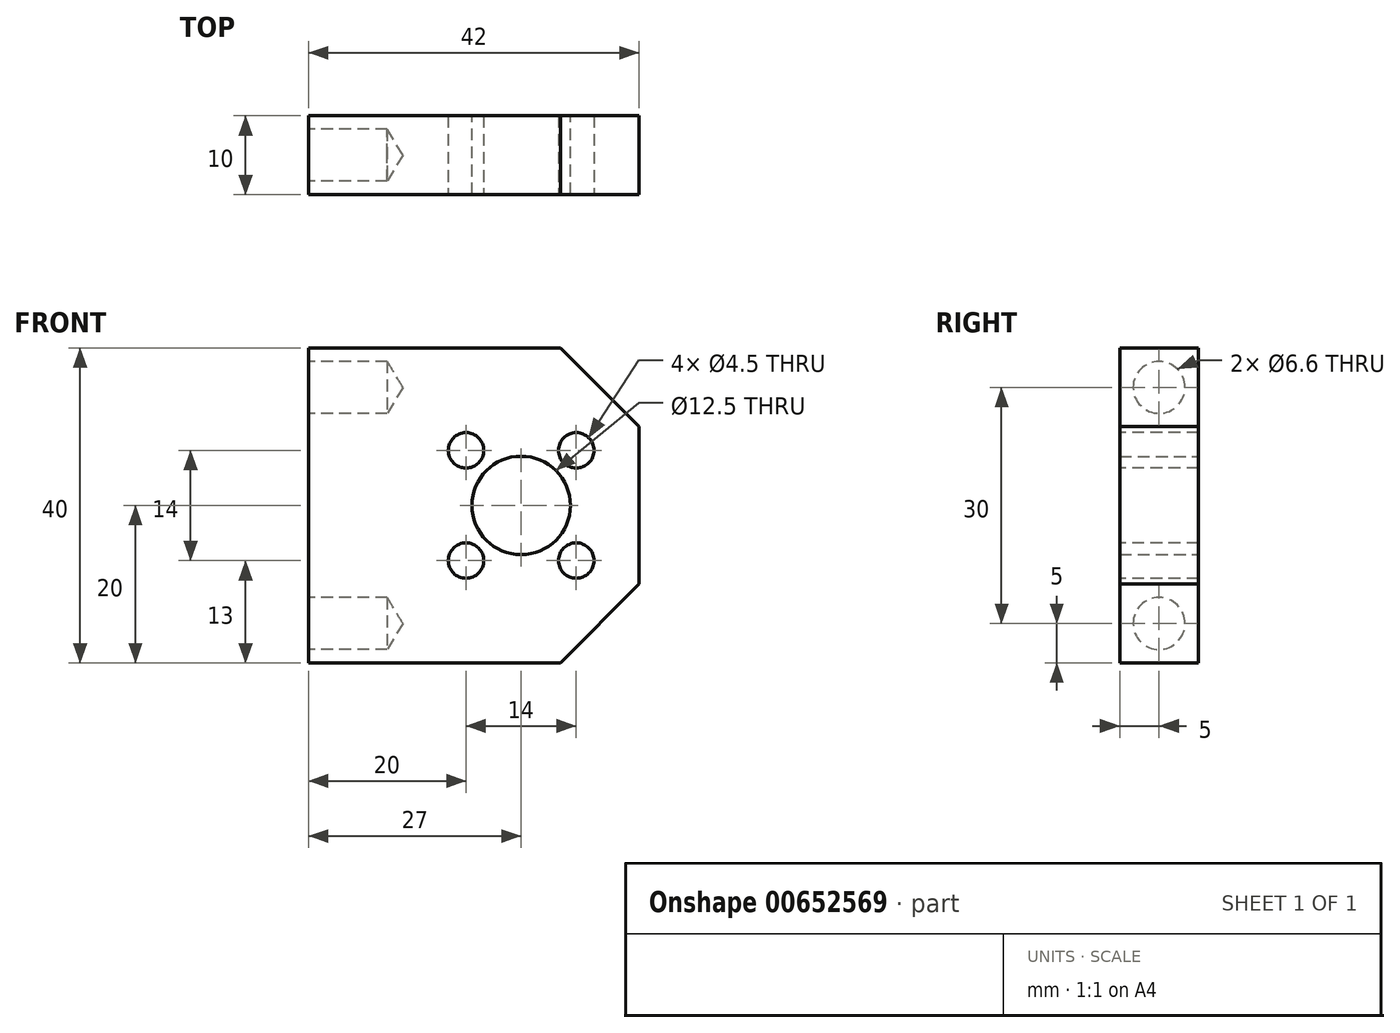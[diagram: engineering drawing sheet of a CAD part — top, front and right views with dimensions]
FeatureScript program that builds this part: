
annotation { "Feature Type Name" : "Feature", "Feature Type Description" : "" }
export const myFeature = defineFeature(function(context is Context, id is Id, definition is map)
    precondition{}
    {
        {
            var Q0;
            Q0=qCreatedBy(makeId("Front.planeOp"),FACE);
            var sketch = newSketch(context, id + "F0", { "sketchPlane" : qUnion([Q0])});
            skLineSegment(sketch, "E0.bottom", {"start": v(21, 20) * mm, "end": v(-21, 20) * mm});
            skLineSegment(sketch, "E0.top", {"start": v(21, -20) * mm, "end": v(-21, -20) * mm});
            skLineSegment(sketch, "E0.left", {"start": v(21, 20) * mm, "end": v(21, -20) * mm});
            skLineSegment(sketch, "E0.right", {"start": v(-21, 20) * mm, "end": v(-21, -20) * mm});
            skPoint(sketch, "E0.middle", {"position": v(0, 0) * mm});
            skCircle(sketch, "E1", {"center": v(6, 0) * mm, "radius": 6.25 * mm});
            skSolve(sketch);
        }
        {
            var Q0;
            Q0 = qSketchRegion(id + "F0", true);
            extrude(context, id + "F1", {"entities" : qUnion([Q0]), "depth" : 10 * mm, "offsetDistance" : 25 * mm});
        }
        {
            var Q0;
            Q0=makeQuery(id+"F1.opExtrude","SWEPT_EDGE",EDGE,{"disambiguationData":[OSD([sQuery(id+"F0.wireOp",EDGE,"E0.bottom"),sQuery(id+"F0.wireOp",EDGE,"E0.left")])]});
            var Q1;
            Q1=makeQuery(id+"F1.opExtrude","SWEPT_EDGE",EDGE,{"disambiguationData":[OSD([sQuery(id+"F0.wireOp",EDGE,"E0.top"),sQuery(id+"F0.wireOp",EDGE,"E0.left")])]});
            chamfer(context, id + "F2", {"entities" : qUnion([Q0, Q1]), "width" : 10 * mm, "tangentPropagation" : true});
        }
        {
            var Q0;
            Q0=makeQuery(id+"F1.opExtrude","CAP_FACE",FACE,{"disambiguationData":[OSD([sQuery(id+"F0.wireOp",EDGE,"E0.bottom"),sQuery(id+"F0.wireOp",EDGE,"E0.top"),sQuery(id+"F0.wireOp",EDGE,"E0.left"),sQuery(id+"F0.wireOp",EDGE,"E0.right"),sQuery(id+"F0.wireOp",EDGE,"E1")])],"isStart":false});
            var sketch = newSketch(context, id + "F3", { "sketchPlane" : qUnion([Q0])});
            skPoint(sketch, "E2", {"position": v(-1, 7) * mm});
            skPoint(sketch, "E3", {"position": v(13, 7) * mm});
            skPoint(sketch, "E4", {"position": v(13, -7) * mm});
            skPoint(sketch, "E5", {"position": v(-1, -7) * mm});
            skSolve(sketch);
        }
        {
            var Q0;
            Q0=sQuery(id+"F3.wireOp",VERTEX,"E2");
            var Q1;
            Q1=sQuery(id+"F3.wireOp",VERTEX,"E5");
            var Q2;
            Q2=sQuery(id+"F3.wireOp",VERTEX,"E4");
            var Q3;
            Q3=sQuery(id+"F3.wireOp",VERTEX,"E3");
            var Q4;
            Q4=makeQuery(id+"F1.opExtrude","SWEPT_BODY",BODY,{"disambiguationData":[OSD([sQuery(id+"F0.wireOp",EDGE,"E0.bottom"),sQuery(id+"F0.wireOp",EDGE,"E0.top"),sQuery(id+"F0.wireOp",EDGE,"E0.left"),sQuery(id+"F0.wireOp",EDGE,"E0.right"),sQuery(id+"F0.wireOp",EDGE,"E1")])]});
            hole(context, id + "F4", {"style" : HoleStyle.SIMPLE, "endStyle" : HoleEndStyle.THROUGH, "holeDiameter" : 4.5 * mm, "majorDiameter" : 5 * mm, "isTappedThrough" : true, "tappedDepth" : 12 * mm, "tapClearance" : 3, "locations" : qUnion([Q0, Q1, Q2, Q3]), "scope" : qUnion([Q4])});
        }
        {
            var Q0;
            Q0=makeQuery(id+"F1.opExtrude","SWEPT_FACE",FACE,{"disambiguationData":[OSD([sQuery(id+"F0.wireOp",EDGE,"E0.right")])]});
            var sketch = newSketch(context, id + "F5", { "sketchPlane" : qUnion([Q0])});
            skPoint(sketch, "E6", {"position": v(5, 15) * mm});
            skPoint(sketch, "E7", {"position": v(5, -15) * mm});
            skSolve(sketch);
        }
        {
            var Q0;
            Q0=sQuery(id+"F5.wireOp",VERTEX,"E6");
            var Q1;
            Q1=sQuery(id+"F5.wireOp",VERTEX,"E7");
            var Q2;
            Q2=makeQuery(id+"F1.opExtrude","SWEPT_BODY",BODY,{"disambiguationData":[OSD([sQuery(id+"F0.wireOp",EDGE,"E0.bottom"),sQuery(id+"F0.wireOp",EDGE,"E0.top"),sQuery(id+"F0.wireOp",EDGE,"E0.left"),sQuery(id+"F0.wireOp",EDGE,"E0.right"),sQuery(id+"F0.wireOp",EDGE,"E1")])]});
            hole(context, id + "F6", {"style" : HoleStyle.SIMPLE, "endStyle" : HoleEndStyle.BLIND, "standardTappedOrClearance" : lookupTablePath({ "standard" : "ISO", "fit" : "Normal", "size" : "M6", "type" : "Clearance" }), "standardBlindInLast" : lookupTablePath({ "fit" : "Standard", "standard" : "ISO", "size" : "M6", "type" : "Clearance" }), "holeDiameter" : 6.6 * mm, "majorDiameter" : 5 * mm, "holeDepth" : 10 * mm, "isTappedThrough" : true, "tappedDepth" : 12 * mm, "tapClearance" : 3, "locations" : qUnion([Q0, Q1]), "scope" : qUnion([Q2])});
        }
    });
